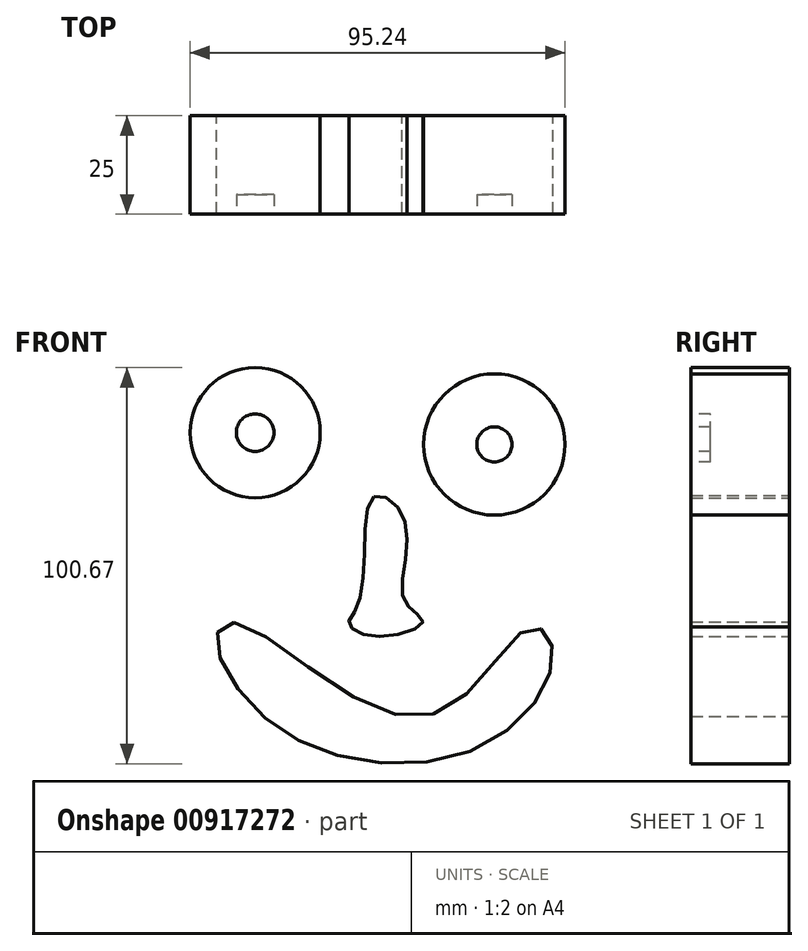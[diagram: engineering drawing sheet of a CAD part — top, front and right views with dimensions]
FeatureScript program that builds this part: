
annotation { "Feature Type Name" : "Feature", "Feature Type Description" : "" }
export const myFeature = defineFeature(function(context is Context, id is Id, definition is map)
    precondition{}
    {
        {
            var Q0;
            Q0=qCreatedBy(makeId("Front.planeOp"),FACE);
            var sketch = newSketch(context, id + "F0", { "sketchPlane" : qUnion([Q0])});
            skCircle(sketch, "E0", {"center": v(-35.88, 37.28) * mm, "radius": 16.54 * mm});
            skCircle(sketch, "E1", {"center": v(24.88, 34.28) * mm, "radius": 17.95 * mm});
            skFitSpline(sketch, "E2", {"points": [v(-41.27, -10.9) * mm, v(-9.1, -30.88) * mm, v(15.5, -31.08) * mm, v(33.28, -12.5) * mm, v(38.68, -14.5) * mm, v(38.28, -25.88) * mm, v(20.29, -43.07) * mm, v(-12.9, -45.27) * mm, v(-37.28, -31.48) * mm, v(-45.67, -14.9) * mm, v(-41.27, -10.9) * mm]});
            skFitSpline(sketch, "E3", {"points": [v(-5.7, 21.09) * mm, v(-8.1, 8.3) * mm, v(-10.1, -7.3) * mm, v(-12.1, -10.9) * mm, v(-9.7, -13.5) * mm, v(0, -14.1) * mm, v(6.7, -10.9) * mm, v(4.5, -8.3) * mm, v(1.5, -3.7) * mm, v(2.7, 8.9) * mm, v(0, 18.69) * mm, v(-5.7, 21.09) * mm]});
            skSolve(sketch);
        }
        {
            var Q0;
            Q0=makeQuery(id+"F0.imprint","IMPRINT",FACE,{"disambiguationData":[TD([[makeQuery(id+"F0.imprint","IMPRINT",EDGE,{"derivedFrom":sQuery(id+"F0.wireOp",EDGE,"E0")}),1.0]])]});
            var Q1;
            Q1=makeQuery(id+"F0.imprint","IMPRINT",FACE,{"disambiguationData":[TD([[makeQuery(id+"F0.imprint","IMPRINT",EDGE,{"derivedFrom":sQuery(id+"F0.wireOp",EDGE,"E1")}),1.0]])]});
            var Q2;
            Q2=makeQuery(id+"F0.imprint","IMPRINT",FACE,{"disambiguationData":[TD([[makeQuery(id+"F0.imprint","IMPRINT",EDGE,{"derivedFrom":sQuery(id+"F0.wireOp",EDGE,"E3")}),1.0]])]});
            var Q3;
            Q3=makeQuery(id+"F0.imprint","IMPRINT",FACE,{"disambiguationData":[TD([[makeQuery(id+"F0.imprint","IMPRINT",EDGE,{"derivedFrom":sQuery(id+"F0.wireOp",EDGE,"E2")}),-1.0]])]});
            extrude(context, id + "F1", {"entities" : qUnion([Q0, Q1, Q2, Q3]), "depth" : 25 * mm, "offsetDistance" : 25 * mm});
        }
        {
            var Q0;
            Q0=makeQuery(id+"F1.opExtrude","CAP_FACE",FACE,{"disambiguationData":[OSD([sQuery(id+"F0.wireOp",EDGE,"E0")])],"isStart":false});
            var sketch = newSketch(context, id + "F2", { "sketchPlane" : qUnion([Q0])});
            skCircle(sketch, "E4", {"center": v(-35.88, 37.28) * mm, "radius": 4.77 * mm});
            skSolve(sketch);
        }
        {
            var Q0;
            Q0=makeQuery(id+"F1.opExtrude","CAP_FACE",FACE,{"disambiguationData":[OSD([sQuery(id+"F0.wireOp",EDGE,"E1")])],"isStart":false});
            var sketch = newSketch(context, id + "F3", { "sketchPlane" : qUnion([Q0])});
            skCircle(sketch, "E5", {"center": v(24.88, 34.28) * mm, "radius": 4.46 * mm});
            skSolve(sketch);
        }
        {
            var Q0;
            Q0=makeQuery(id+"F2.imprint","IMPRINT",FACE,{"disambiguationData":[TD([[makeQuery(id+"F2.imprint","IMPRINT",EDGE,{"derivedFrom":sQuery(id+"F2.wireOp",EDGE,"E4")}),1.0]])]});
            var Q1;
            Q1=makeQuery(id+"F3.imprint","IMPRINT",FACE,{"disambiguationData":[TD([[makeQuery(id+"F3.imprint","IMPRINT",EDGE,{"derivedFrom":sQuery(id+"F3.wireOp",EDGE,"E5")}),1.0]])]});
            extrude(context, id + "F4", {"entities" : qUnion([Q0, Q1]), "depth" : -5 * mm, "offsetDistance" : 25 * mm});
        }
        {
            var Q0;
            Q0=makeQuery(id+"F4.opExtrude","CAP_FACE",FACE,{"disambiguationData":[OSD([sQuery(id+"F2.wireOp",EDGE,"E4")])],"isStart":true});
            extrude(context, id + "F5", {"entities" : qUnion([Q0]), "depth" : -5 * mm, "offsetDistance" : 25 * mm});
        }
    });
